# Revit family: Bi-level_ADA_Cooler_Non-filtered-Elkay-VRCTLFR8SC
name_source: partatom
category: Plumbing Fixtures
units: mm (PartAtom-declared; Revit-internal decimal feet)

## family parameters
Always vertical = Yes
Cut with Voids When Loaded = No
Maintain Annotation Orientation = No
OmniClass Number = 23.65.70.14.11
OmniClass Title = Drinking Fountains/Coolers
Part Type = Normal
Room Calculation Point = No
Round Connector Dimension = Use Diameter
Shared = No
Work Plane-Based = No

## types (1)
- VRCTLFR8SC (Vandal Resistant Bi-level ADA Cooler Non-filtered Refrigerated Stainless )
    Activation Method = Mechanical Front Bubbler Button
    Approx. Shipping Weight (lbs) = 94
    Assembly Code = D2010.60
    CWFU = 0
    Chilling Capacity (GPH) = 8
    Connector Outlet B = 1.5 "
    Connector Supply A = 0.375 "
    Current = 0 A
    Default Elevation = 0 "
    Description = Wall Mount Vandal Resistant Bi-level ADA Cooler Frost Resistant Non-filtered Refrigerated Stainless
    Dimensions (L x W x H) = 36 5/16 inch x 18 5/8 inch x 27 1/8 inch
    Floor to waste outlet = 18.75 "
    Floor to water supply loaction = 20.125 "
    HWFU = 0
    Inlet Connection Size (inch) = 0.375 "
    Installation Location = Indoor + Outdoor
    Main Material = Elkay-Stainless Steel
    Manufacturer = Elkay Manufacturer Company
    Manufacturer Brand = Elkay (by Zurn Elkay Water Solutions)
    Model = VRCTLFR8SC
    Number of Poles = 1
    Outlet Connection Size (inch) = 1.5 "
    Power Factor = 1
    Product Documentation Link = https://www.elkayfiles.com
    Product Installation Sheet URL = https://www.elkayfiles.com
    Product Page URL = https://www.elkay.com
    Product Weight (lbs) = 76
    Product data URL = https://www.bimobject.com
    Repair Parts URL = https://www.elkayfiles.com
    URL = https://www.elkay.com
    Voltage = 115 V
    WFU = 0

## geometry (parser evidence)
native form markers: Sweep x13
no freeform markers — native parametric forms only
